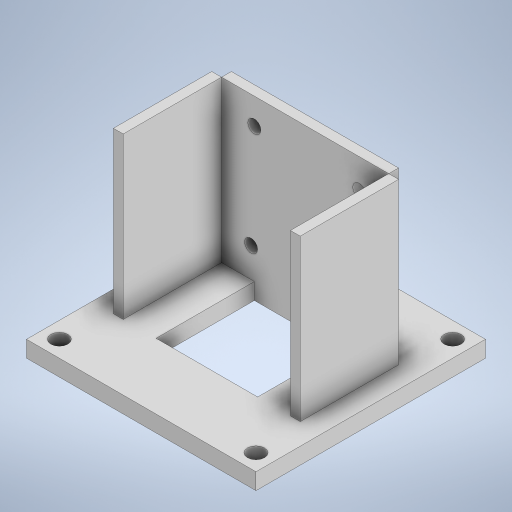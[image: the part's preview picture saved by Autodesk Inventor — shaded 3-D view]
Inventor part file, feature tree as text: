
AUTODESK INVENTOR PART (.ipt)
format: ipt  version: 2024 (Build 280153000, 153)  size: 327,168 bytes
history: native  units: mm
features: extrude x6, sketch x6, other x1
ambient origin geometry x8: Origin, YZ Plane, XZ Plane, XY Plane, X Axis, Y Axis, Z Axis, Center Point
bodies: Body1 (feature_tree)
feature tree (13):
  other  "Sólido1"
  extrude  "Extrusión1"  Depth=5.0mm TaperAngle=0.0deg
  extrude  "Extrusión4"  Depth=30.0mm
  extrude  "Extrusión5"  Depth=57.0mm
  extrude  "Extrusión6"  TaperAngle=0.0deg  [1 undecoded]
  extrude  "Extrusión7"  Depth=49.0mm
  extrude  "Extrusión10"  Depth=5.0mm
  sketch  "Boceto1"  dims[d2=10.0mm d7=5.0mm d8=0.0mm]
  sketch  "Boceto4"  dims[d21=51.0mm d22=30.0mm]
  sketch  "Boceto5"  dims[d23=57.0mm d24=36.0mm]
  sketch  "Boceto6"  dims[d25=5.0mm d26=0.0mm d27=0.0mm]
  sketch  "Boceto7"  dims[d28=49.0mm d29=0.0mm d30=4.0mm]
  sketch  "Boceto12"  dims[d31=9.0mm d32=9.0mm d33=40.0mm d35=360.0deg d37=49.0mm d38=0.0mm d39=49.0mm d40=0.0mm d63=70.0mm d64=70.0mm d65=60.0mm d66=5.2mm d67=5.2mm d68=5.2mm d69=5.2mm d70=5.0mm d71=0.0mm]
note: 1 required parameter value undecoded (feature->parameter linkage not recoverable at this tier; creation-order binding heuristic only, values carry confidence <= 0.55)
